# Revit family: Plumbing-Faucet-Sloan-Valve-ETF-500
name_source: partatom
category: Plumbing Fixtures
units: mm (PartAtom-declared; Revit-internal decimal feet)

## family parameters
Cut with Voids When Loaded = No
Host = Face
OmniClass Number = 23.45.55.14
OmniClass Title = Single Faucets
Part Type = Normal
Room Calculation Point = No
Round Connector Dimension = Use Diameter
Shared = No

## types (23) — shared parameters
Apparent Load = 0 VA
Assembly Code = D2010
CW Connection = Yes
CWFU = 1.5
Connector Description = Electrical Connection
Current = 0 A
Default Elevation = 0"
Edition number = 1
HW Connection = Yes
HWFU = 1.5
Keynote = 15410
Manufacturer = Sloan Valve
Number of Poles = 1
Power Factor = 1
Product Material = Sloan Valve - Finish - Polished Chrome
Product data url = https://bimobject.com
URL = www.sloanvalve.com
Valve Pressure Drop = 0.00 psi
Vent Connection = No
Waste Connection = No
Water Flow = 2 GPM
Water Inlet Connection Description = Pretempered Water Supply Connection
Water Inlet Connection Diameter = 0"
Width = 5 7/8"
zero-valued in all types: WFU

## per-type parameters (varying)
| type | Depth | Description | Height | Part Number | Voltage | z_Body Type 1- Big | z_Body Type 1- Small | z_Body Type 2- Big | z_Body Type 2- Small | z_LAM Big | z_LAM Small | z_SHR Big | z_SHR Small |
| ETF-500-BOX-BDM-CP-1.5GPM-SHR-IR-FCT | 7 3/4" | Box Transformer Power Supply, Below Deck Manual Mixing Valve, Polished Chrome Finish, 1.5 gpm, Shower Head Spray, Infrared Sensor, Optima® Hardwired-Powered Wall-Mounted Gooseneck Body. | 10 1/4" | 3365378BT | 24 V | No | Yes | No | No | No | No | No | Yes |
| ETF-500-BOX-BDM-CP-1.5GPM-SHR-IR-S-FCT | 9 3/8" | Box Transformer Power Supply, Below Deck Manual Mixing Valve, Polished Chrome Finish, 1.5 gpm, Shower Head Spray, Infrared Sensor, Optima® Hardwired-Powered Wall-Mounted Gooseneck Body. | 12 3/8" | 3365357BT | 24 V | No | No | No | Yes | No | No | Yes | No |
| ETF-500-BOX-BDM-CP-2.2GPM-LAM-IR-FCT | 7 3/4" | Box Transformer Power Supply, Below Deck Manual Mixing Valve, Polished Chrome Finish, 2.2 gpm, Laminar Spray, Infrared Sensor, Optima® Hardwired-Powered Wall-Mounted Gooseneck Body. | 14 1/4" | 3365367BT | 24 V | Yes | No | No | No | No | Yes | No | No |
| ETF-500-BOX-BDM-CP-2.2GPM-LAM-IR-S-FCT | 9 3/8" | Box Transformer Power Supply, Below Deck Manual Mixing Valve, Polished Chrome Finish, 2.2 gpm, Laminar Spray, Infrared Sensor, Optima® Hardwired-Powered Wall-Mounted Gooseneck Body. | 12 3/8" | 3365346BT | 24 V | No | No | No | Yes | Yes | No | No | No |
| ETF-500-BOX-BDT-CP-1.5GPM-SHR-IR-FCT | 7 3/4" | Box Transformer Power Supply, Below Deck Thermostatic Mixing Valve, Polished Chrome Finish, 1.5 gpm, Shower Head Spray, Infrared Sensor, Optima® Hardwired-Powered Wall-Mounted Gooseneck Body. | 10 1/4" | 3365239BT | 24 V | No | Yes | No | No | No | No | No | Yes |
| TF-500-BOX-BDT-CP-1.5GPM-SHR-IR-S-FCT | 9 3/8" | Box Transformer Power Supply, Below Deck Thermostatic Mixing Valve, Polished Chrome Finish, 1.5 gpm, Shower Head Spray, Infrared Sensor, Optima® Hardwired-Powered Wall-Mounted Gooseneck Body. | 12 3/8" | 3365245BT | 24 V | No | No | No | Yes | No | No | Yes | No |
| ETF-500-BOX-BDT-CP-2.2GPM-LAM-IR-FCT | 7 3/4" | Box Transformer Power Supply, Below Deck Thermostatic Mixing Valve, Polished Chrome Finish, 2.2 gpm, Laminar Spray, Infrared Sensor, Optima® Hardwired-Powered Wall-Mounted Gooseneck Body. | 14 1/4" | 3365236BT | 24 V | Yes | No | No | No | No | Yes | No | No |
| ETF-500-BOX-BDT-CP-2.2GPM-LAM-IR-S-FCT | 9 3/8" | Box Transformer Power Supply, Below Deck Thermostatic Mixing Valve, Polished Chrome Finish, 2.2 gpm, Laminar Spray, Infrared Sensor, Optima® Hardwired-Powered Wall-Mounted Gooseneck Body. | 16 3/8" | 3365242BT | 24 V | No | No | Yes | No | Yes | No | No | No |
| ETF-500-BOX-TEE-CP-1.5GPM-SHR-IR-FCT | 7 3/4" | Box Transformer Power Supply, Back-Check Tee, Polished Chrome Finish, 1.5 gpm, Shower Head Spray, Infrared Sensor, Optima® Hardwired-Powered Wall-Mounted Gooseneck Body. | 10 1/4" | 3365343BT | 24 V | No | Yes | No | No | No | No | No | Yes |
| ETF-500-BOX-TEE-CP-2.2GPM-LAM-IR-FCT | 7 3/4" | Box Transformer Power Supply, Back-Check Tee, Polished Chrome Finish, 2.2 gpm, Laminar Spray, Infrared Sensor, Optima® HardwiredPowered Wall-Mounted Gooseneck Body. | 14 1/4" | 3365341BT | 24 V | Yes | No | No | No | No | Yes | No | No |
| ETF-500-BOX-TEE-CP-2.2GPM-LAM-IR-S-FCT | 9 3/8" | Box Transformer Power Supply, Back-Check Tee, Polished Chrome Finish, 2.2 gpm, Laminar Spray, Infrared Sensor, Optima® HardwiredPowered Wall-Mounted Gooseneck Body. | 12 3/8" | 3365336BT | 24 V | No | No | No | Yes | Yes | No | No | No |
| ETF-500-PLG-BDM-CP-1.5GPM-SHR-IR-FCT | 7 3/4" | Plug Adapter Power Supply, Below Deck Manual Mixing Valve, Polished Chrome Finish, 1.5 gpm, Shower Head Spray, Infrared Sensor, Optima® Hardwired-Powered Wall-Mounted Gooseneck Body. | 10 1/4" | 3365374BT | 6 V | No | Yes | No | No | No | No | No | Yes |
| ETF-500-PLG-BDM-CP-1.5GPM-SHR-IR-S-FCT | 9 3/8" | Plug Adapter Power Supply, Below Deck Manual Mixing Valve, Polished Chrome Finish, 1.5 gpm, Shower Head Spray, Infrared Sensor, Optima® Hardwired-Powered Wall-Mounted Gooseneck Body. | 12 3/8" | 3365353BT | 6 V | No | No | No | Yes | No | No | Yes | No |
| ETF-500-PLG-BDM-CP-2.2GPM-LAM-IR-FCT | 7 3/4" | Plug Adapter Power Supply, Below Deck Manual Mixing Valve, Polished Chrome Finish, 2.2 gpm, Laminar Spray, Infrared Sensor, Optima® Hardwired-Powered Wall-Mounted Gooseneck Body. | 14 1/4" | 3365364BT | 6 V | Yes | No | No | No | No | Yes | No | No |
| ETF-500-PLG-BDM-CP-2.2GPM-LAM-IR-S-FCT | 9 3/8" | Plug Adapter Power Supply, Below Deck Manual Mixing Valve, Polished Chrome Finish, 2.2 gpm, Laminar Spray, Infrared Sensor, Optima® Hardwired-Powered Wall-Mounted Gooseneck Body | 12 3/8" | 3365345BT | 6 V | No | No | No | Yes | Yes | No | No | No |
| ETF-500-PLG-BDT-CP-1.5GPM-SHR-IR-FCT | 7 3/4" | Plug Adapter Power Supply, Below Deck Thermostatic Mixing Valve, Polished Chrome Finish, 1.5 gpm, Shower Head Spray, Infrared Sensor, Optima® Hardwired-Powered Wall-Mounted Gooseneck Body. | 10 1/4" | 3365238BT | 6 V | No | Yes | No | No | No | No | No | Yes |
| ETF-500-PLG-BDT-CP-1.5GPM-SHR-IR-S-FCT | 9 3/8" | Plug Adapter Power Supply, Below Deck Thermostatic Mixing Valve, Polished Chrome Finish, 1.5 gpm, Shower Head Spray, Infrared Sensor, Optima® Hardwired-Powered Wall-Mounted Gooseneck Body. | 12 3/8" | 3365244BT | 6 V | No | No | No | Yes | No | No | Yes | No |
| ETF-500-PLG-BDT-CP-2.2GPM-LAM-IR-FCT | 7 3/4" | Plug Adapter Power Supply, Below Deck Thermostatic Mixing Valve, Polished Chrome Finish, 2.2 gpm, Laminar Spray, Infrared Sensor, Optima® Hardwired-Powered Wall-Mounted Gooseneck Body. | 14 1/4" | 3365235BT | 6 V | Yes | No | No | No | No | Yes | No | No |
| ETF-500-PLG-BDT-CP-2.2GPM-LAM-IR-S-FCT | 9 3/8" | Plug Adapter Power Supply, Below Deck Thermostatic Mixing Valve, Polished Chrome Finish, 2.2 gpm, Laminar Spray, Infrared Sensor, Optima® Hardwired-Powered Wall-Mounted Gooseneck Body. | 12 3/8" | 3365241BT | 6 V | No | No | No | Yes | Yes | No | No | No |
| ETF-500-PLG-TEE-CP-1.5GPM-SHR-IR-FCT | 7 3/4" | Plug Adapter Power Supply, Back-Check Tee, Polished Chrome Finish, 1.5 gpm, Shower Head Spray, Infrared Sensor, Optima® HardwiredPowered Wall-Mounted Gooseneck Body. | 10 1/4" | 3365342BT | 6 V | No | Yes | No | No | No | No | No | Yes |
| ETF-500-PLG-TEE-CP-1.5GPM-SHR-IR-S-FCT | 9 3/8" | Plug Adapter Power Supply, Back-Check Tee, Polished Chrome Finish, 1.5 gpm, Shower Head Spray, Infrared Sensor, Optima® HardwiredPowered Wall-Mounted Gooseneck Body. | 12 3/8" | 3365337BT | 6 V | No | No | No | Yes | No | No | Yes | No |
| ETF-500-PLG-TEE-CP-2.2GPM-LAM-IR-FCT | 7 3/4" | Plug Adapter Power Supply, Back-Check Tee, Polished Chrome Finish, 2.2 gpm, Laminar Spray, Infrared Sensor, Optima® HardwiredPowered Wall-Mounted Gooseneck Body. | 14 1/4" | 3365340BT | 6 V | Yes | No | No | No | No | Yes | No | No |
| ETF-500-PLG-TEE-CP-2.2GPM-LAM-IR-S-FCT | 9 3/8" | Plug Adapter Power Supply, Back-Check Tee, Polished Chrome Finish, 2.2 gpm, Laminar Spray, Infrared Sensor, Optima® HardwiredPowered Wall-Mounted Gooseneck Body. | 12 3/8" | 3365335BT | 6 V | No | No | No | Yes | Yes | No | No | No |

note: column(s) folded — value = type name in every type: Model

## geometry (parser evidence)
native form markers: Sweep x4
no freeform markers — native parametric forms only
